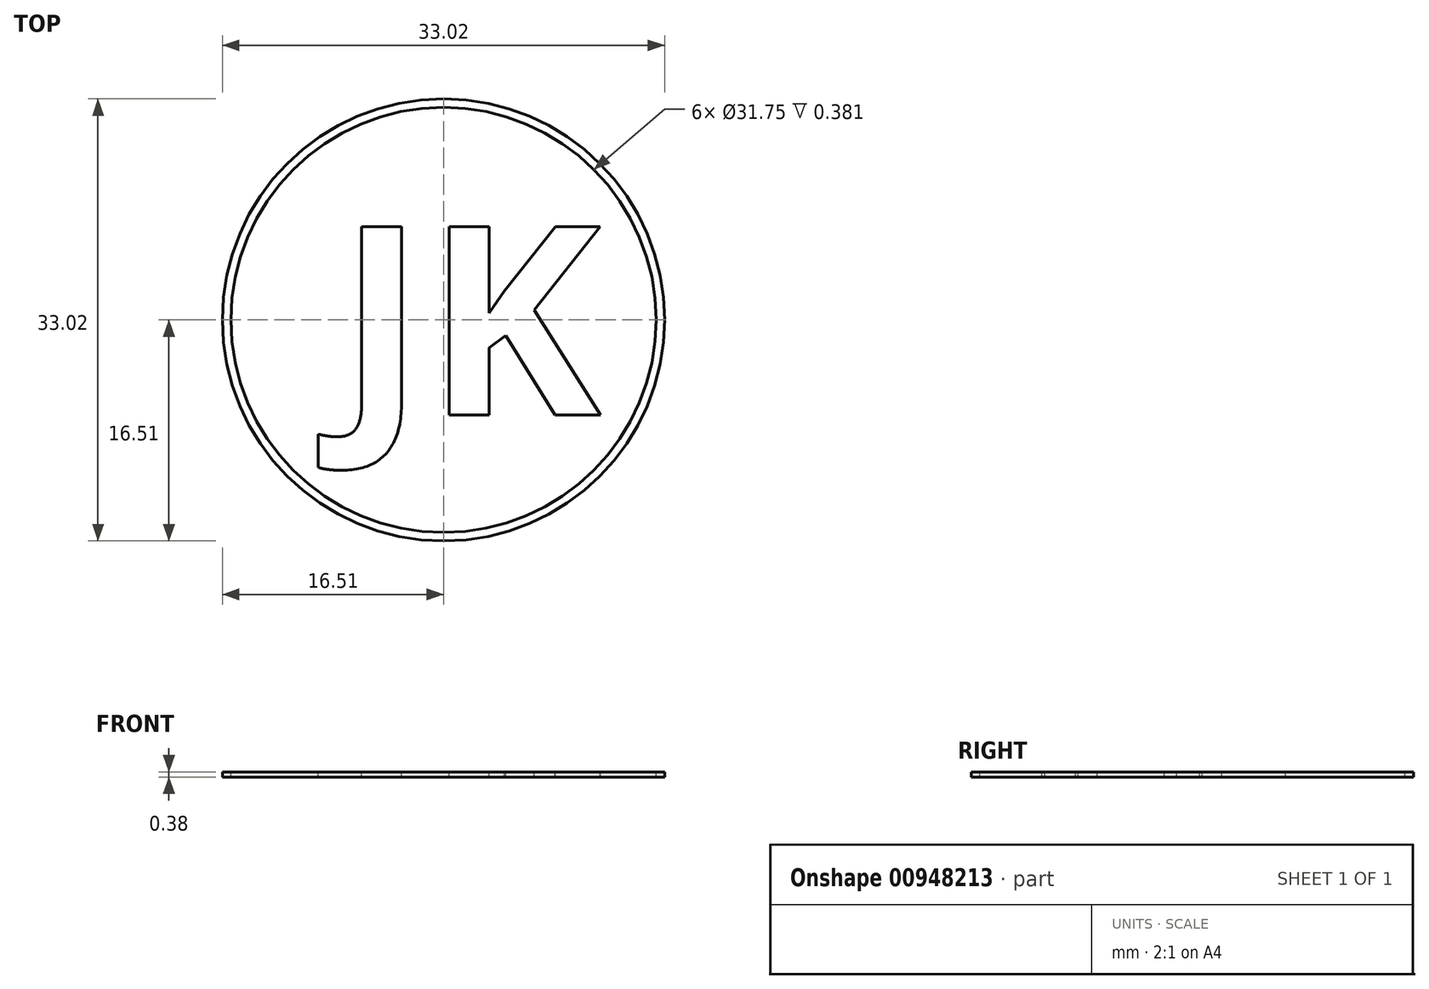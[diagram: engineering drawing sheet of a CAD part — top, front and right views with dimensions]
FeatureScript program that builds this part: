
annotation { "Feature Type Name" : "Feature", "Feature Type Description" : "" }
export const myFeature = defineFeature(function(context is Context, id is Id, definition is map)
    precondition{}
    {
        {
            var Q0;
            Q0=qCreatedBy(makeId("Top.planeOp"),FACE);
            cPlane(context, id + "F0", {"entities" : qUnion([Q0]), "cplaneType" : CPlaneType.OFFSET, "offset" : 3.3 * mm, "width" : 152.4 * mm, "height" : 152.4 * mm});
        }
        {
            var Q0;
            Q0=qCreatedBy(id+"F0.planeOp",FACE);
            var sketch = newSketch(context, id + "F1", { "sketchPlane" : qUnion([Q0])});
            skText(sketch, "E0", { "text": " JK", "fontName": "OpenSans-Bold.ttf"});
            const initialGuessF1  = {"E0": [-0.013, -0.0071, 1, 0, 0.01418]};
            skSetInitialGuess(sketch, initialGuessF1);
            skSolve(sketch);
        }
        {
            var Q0;
            Q0=qCreatedBy(id+"F0.planeOp",FACE);
            var sketch = newSketch(context, id + "F2", { "sketchPlane" : qUnion([Q0])});
            skCircle(sketch, "E1", {"center": v(0, 0) * mm, "radius": 15.88 * mm});
            skCircle(sketch, "E2", {"center": v(0, 0) * mm, "radius": 16.51 * mm});
            skSolve(sketch);
        }
        {
            var Q0;
            Q0=qSketchRegion(id+"F1",true);
            var Q1;
            Q1=qSketchRegion(id+"F2",true);
            extrude(context, id + "F3", {"entities" : qUnion([Q0, Q1]), "oppositeDirection" : true, "depth" : 0.38 * mm, "offsetDistance" : 25.4 * mm});
        }
    });
